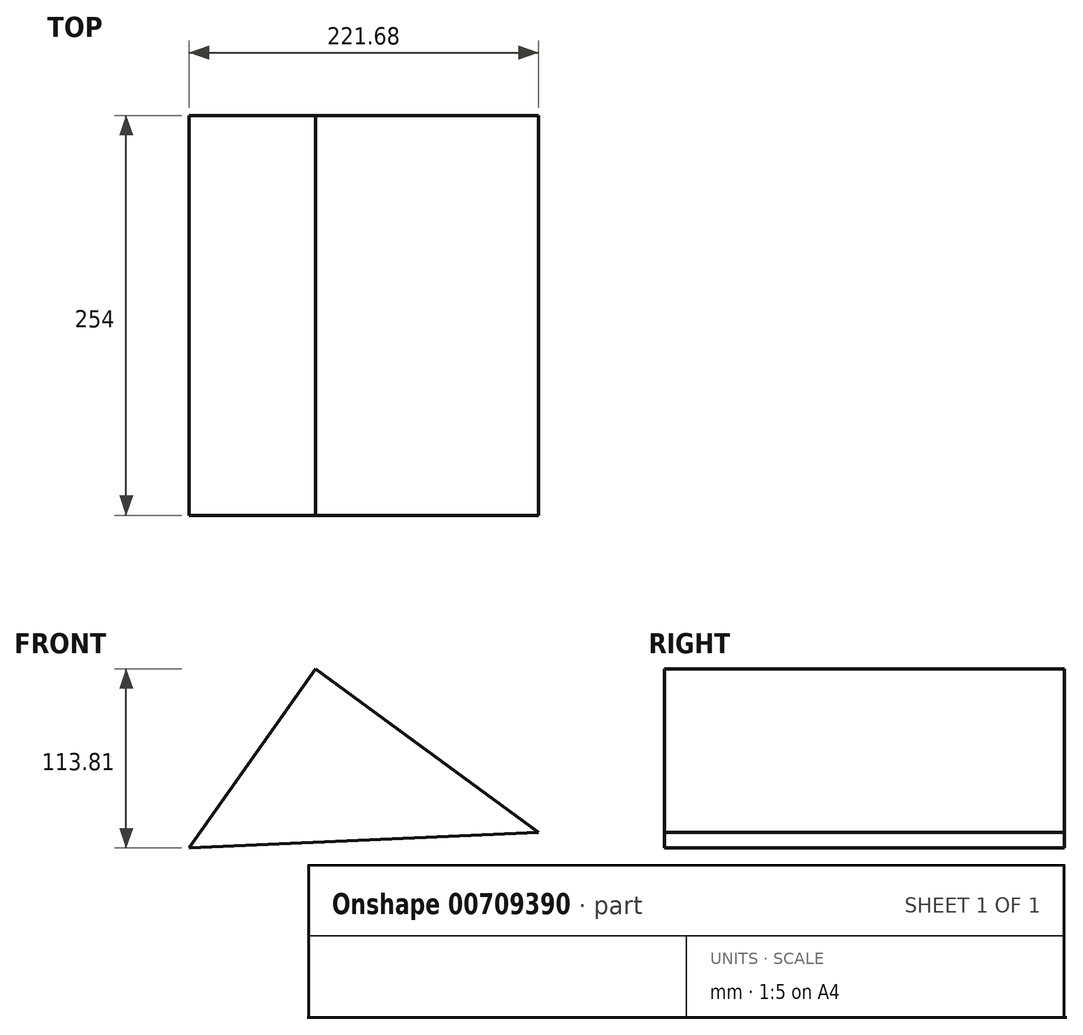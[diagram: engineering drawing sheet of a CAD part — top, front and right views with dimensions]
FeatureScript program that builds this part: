
annotation { "Feature Type Name" : "Feature", "Feature Type Description" : "" }
export const myFeature = defineFeature(function(context is Context, id is Id, definition is map)
    precondition{}
    {
        {
            var Q0;
            Q0=qCreatedBy(makeId("Front.planeOp"),FACE);
            var sketch = newSketch(context, id + "F0", { "sketchPlane" : qUnion([Q0])});
            skLineSegment(sketch, "E0", {"start": v(-71, 50.78) * mm, "end": v(70.6, -53.1) * mm});
            skLineSegment(sketch, "E1", {"start": v(0, -1.3) * mm, "end": v(-151.07, -63.03) * mm});
            skLineSegment(sketch, "E2", {"start": v(-151.07, -63.03) * mm, "end": v(-71, 50.78) * mm});
            skLineSegment(sketch, "E3", {"start": v(-151.07, -63.03) * mm, "end": v(70.6, -53.1) * mm});
            skSolve(sketch);
        }
        {
            var Q0;
            {var subQ2=sQuery(id+"F0.wireOp",EDGE,"E1");Q0=makeQuery(id+"F0.imprint","IMPRINT",FACE,{"disambiguationData":[TD([[makeQuery(id+"F0.imprint","IMPRINT",EDGE,{"derivedFrom":subQ2}),-1.0]])]});}
            var Q1;
            {var subQ2=sQuery(id+"F0.wireOp",EDGE,"E1");Q1=makeQuery(id+"F0.imprint","IMPRINT",FACE,{"disambiguationData":[TD([[makeQuery(id+"F0.imprint","IMPRINT",EDGE,{"derivedFrom":subQ2}),1.0]])]});}
            extrude(context, id + "F1", {"entities" : qUnion([Q0, Q1]), "depth" : 254 * mm, "offsetDistance" : 25.4 * mm});
        }
    });
